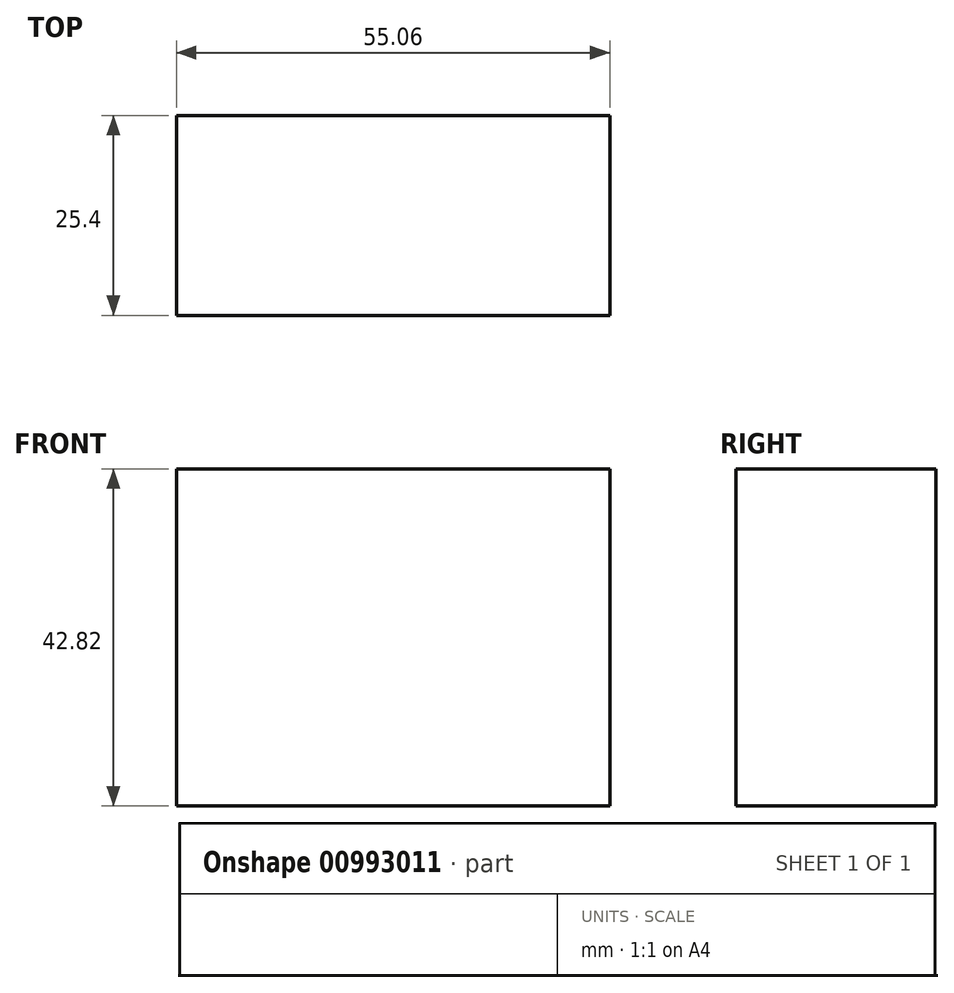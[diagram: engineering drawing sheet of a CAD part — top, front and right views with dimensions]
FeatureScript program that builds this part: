
annotation { "Feature Type Name" : "Feature", "Feature Type Description" : "" }
export const myFeature = defineFeature(function(context is Context, id is Id, definition is map)
    precondition{}
    {
        {
            var Q0;
            Q0=qCreatedBy(makeId("Front.planeOp"),FACE);
            var sketch = newSketch(context, id + "F0", { "sketchPlane" : qUnion([Q0])});
            skLineSegment(sketch, "E0.bottom", {"start": v(-51.38, 34.18) * mm, "end": v(3.68, 34.18) * mm});
            skLineSegment(sketch, "E0.top", {"start": v(-51.38, -8.64) * mm, "end": v(3.68, -8.64) * mm});
            skLineSegment(sketch, "E0.left", {"start": v(-51.38, 34.18) * mm, "end": v(-51.38, -8.64) * mm});
            skLineSegment(sketch, "E0.right", {"start": v(3.68, 34.18) * mm, "end": v(3.68, -8.64) * mm});
            skSolve(sketch);
        }
        {
            var Q0;
            Q0=makeQuery(id+"F0.imprint","IMPRINT",FACE,{"disambiguationData":[TD([[makeQuery(id+"F0.imprint","IMPRINT",EDGE,{"derivedFrom":sQuery(id+"F0.wireOp",EDGE,"E0.bottom")}),-1.0]])]});
            extrude(context, id + "F1", {"entities" : qUnion([Q0]), "depth" : 25.4 * mm, "offsetDistance" : 25.4 * mm});
        }
    });
